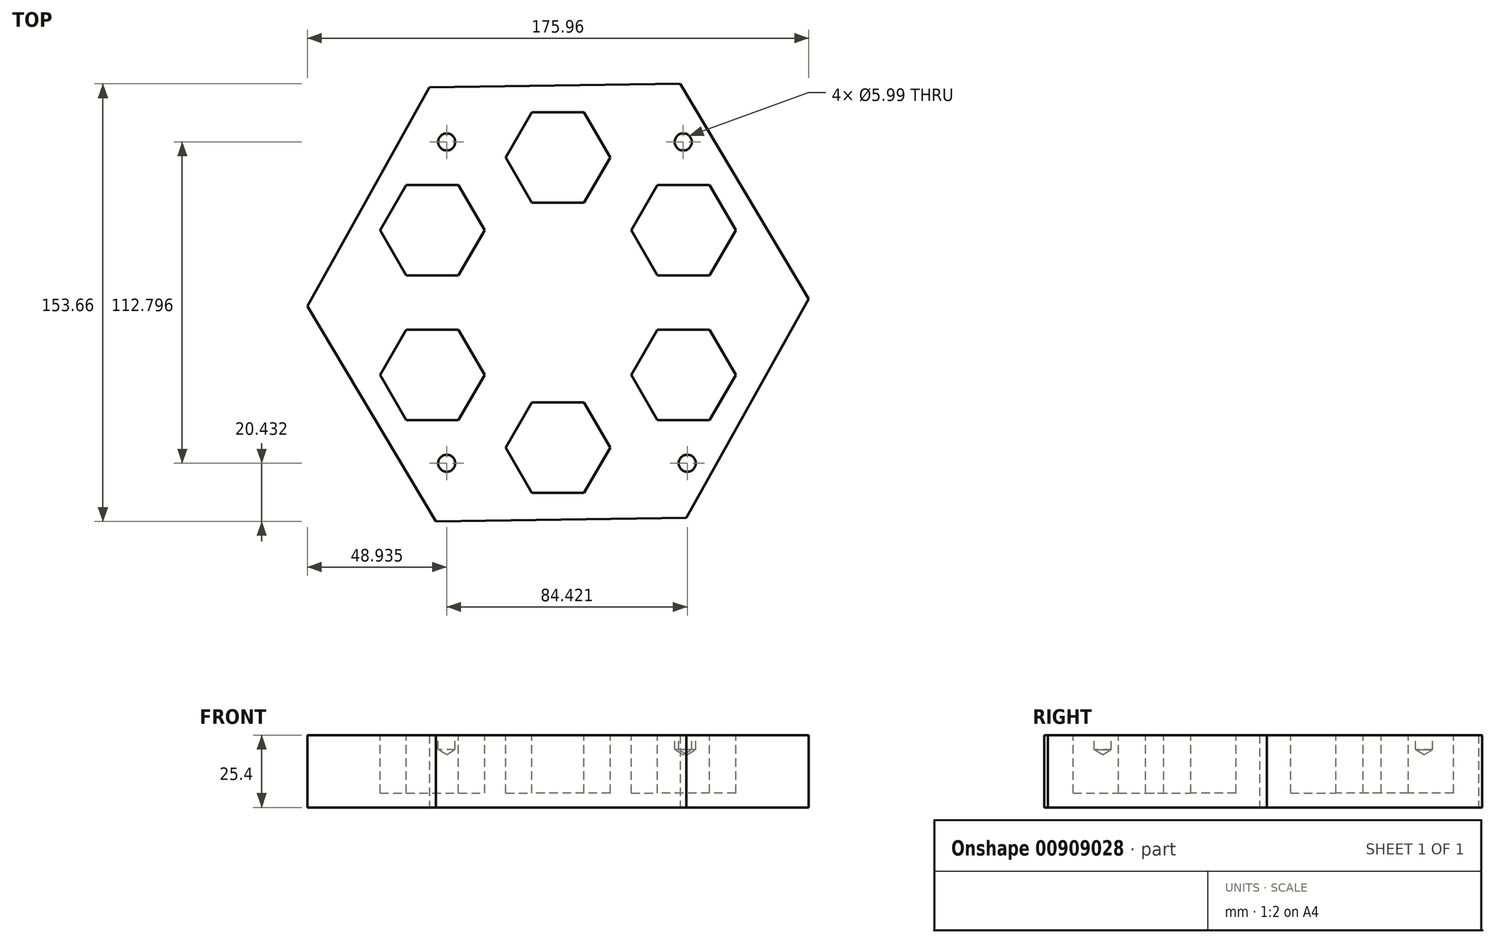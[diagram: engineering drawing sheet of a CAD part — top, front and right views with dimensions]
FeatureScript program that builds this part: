
annotation { "Feature Type Name" : "Feature", "Feature Type Description" : "" }
export const myFeature = defineFeature(function(context is Context, id is Id, definition is map)
    precondition{}
    {
        {
            var Q0;
            Q0=qCreatedBy(makeId("Top.planeOp"),FACE);
            var sketch = newSketch(context, id + "F0", { "sketchPlane" : qUnion([Q0])});
            skCircle(sketch, "E0.cCircle", {"center": v(0, 0) * mm, "radius": 76.2 * mm, "construction": true});
            skLineSegment(sketch, "E0.0", {"start": v(87.98, 1.27) * mm, "end": v(45.1, -75.56) * mm});
            skLineSegment(sketch, "E0.1", {"start": v(45.1, -75.56) * mm, "end": v(-42.89, -76.83) * mm});
            skLineSegment(sketch, "E0.2", {"start": v(-42.89, -76.83) * mm, "end": v(-87.98, -1.27) * mm});
            skLineSegment(sketch, "E0.3", {"start": v(-87.98, -1.27) * mm, "end": v(-45.1, 75.56) * mm});
            skLineSegment(sketch, "E0.4", {"start": v(-45.1, 75.56) * mm, "end": v(42.89, 76.83) * mm});
            skLineSegment(sketch, "E0.5", {"start": v(42.89, 76.83) * mm, "end": v(87.98, 1.27) * mm});
            skPoint(sketch, "E0.0.midPoint", {"position": v(66.53, -37.14) * mm});
            skSolve(sketch);
        }
        {
            var Q0;
            Q0=makeQuery(id+"F0.imprint","IMPRINT",FACE,{"disambiguationData":[TD([[makeQuery(id+"F0.imprint","IMPRINT",EDGE,{"derivedFrom":sQuery(id+"F0.wireOp",EDGE,"E0.0")}),-1.0]])]});
            extrude(context, id + "F1", {"entities" : qUnion([Q0]), "depth" : 25.4 * mm, "offsetDistance" : 25.4 * mm});
        }
        {
            var Q0;
            Q0=makeQuery(id+"F1.opExtrude","CAP_FACE",FACE,{"disambiguationData":[OSD([sQuery(id+"F0.wireOp",EDGE,"E0.0"),sQuery(id+"F0.wireOp",EDGE,"E0.1"),sQuery(id+"F0.wireOp",EDGE,"E0.2"),sQuery(id+"F0.wireOp",EDGE,"E0.3"),sQuery(id+"F0.wireOp",EDGE,"E0.4"),sQuery(id+"F0.wireOp",EDGE,"E0.5")])],"isStart":false});
            var sketch = newSketch(context, id + "F2", { "sketchPlane" : qUnion([Q0])});
            skCircle(sketch, "E1.cCircle", {"center": v(0, 50.9) * mm, "radius": 15.88 * mm, "construction": true});
            skLineSegment(sketch, "E1.0", {"start": v(9.17, 35.02) * mm, "end": v(-9.17, 35.02) * mm});
            skLineSegment(sketch, "E1.1", {"start": v(-9.17, 35.02) * mm, "end": v(-18.33, 50.9) * mm});
            skLineSegment(sketch, "E1.2", {"start": v(-18.33, 50.9) * mm, "end": v(-9.17, 66.77) * mm});
            skLineSegment(sketch, "E1.3", {"start": v(-9.17, 66.77) * mm, "end": v(9.17, 66.77) * mm});
            skLineSegment(sketch, "E1.4", {"start": v(9.17, 66.77) * mm, "end": v(18.33, 50.9) * mm});
            skLineSegment(sketch, "E1.5", {"start": v(18.33, 50.9) * mm, "end": v(9.17, 35.02) * mm});
            skPoint(sketch, "E1.0.midPoint", {"position": v(0, 35.02) * mm});
            skPoint(sketch, "E2", {"position": v(-1.1, 76.2) * mm});
            skLineSegment(sketch, "E3.1.0", {"start": v(-34.9, 41.32) * mm, "end": v(-25.74, 25.45) * mm});
            skLineSegment(sketch, "E3.1.1", {"start": v(-53.24, 41.32) * mm, "end": v(-34.9, 41.32) * mm});
            skLineSegment(sketch, "E3.1.2", {"start": v(-62.4, 25.45) * mm, "end": v(-53.24, 41.32) * mm});
            skLineSegment(sketch, "E3.1.3", {"start": v(-53.24, 9.57) * mm, "end": v(-62.4, 25.45) * mm});
            skLineSegment(sketch, "E3.1.4", {"start": v(-34.9, 9.57) * mm, "end": v(-53.24, 9.57) * mm});
            skPoint(sketch, "E3.1.5", {"position": v(-30.33, 17.5) * mm});
            skCircle(sketch, "E3.1.6", {"center": v(-44.07, 25.45) * mm, "radius": 15.88 * mm, "construction": true});
            skLineSegment(sketch, "E3.1.7", {"start": v(-25.74, 25.45) * mm, "end": v(-34.9, 9.57) * mm});
            skLineSegment(sketch, "E3.2.0", {"start": v(-53.24, -9.57) * mm, "end": v(-34.9, -9.57) * mm});
            skLineSegment(sketch, "E3.2.1", {"start": v(-62.4, -25.45) * mm, "end": v(-53.24, -9.57) * mm});
            skLineSegment(sketch, "E3.2.2", {"start": v(-53.24, -41.32) * mm, "end": v(-62.4, -25.45) * mm});
            skLineSegment(sketch, "E3.2.3", {"start": v(-34.9, -41.32) * mm, "end": v(-53.24, -41.32) * mm});
            skLineSegment(sketch, "E3.2.4", {"start": v(-25.74, -25.45) * mm, "end": v(-34.9, -41.32) * mm});
            skPoint(sketch, "E3.2.5", {"position": v(-30.33, -17.5) * mm});
            skCircle(sketch, "E3.2.6", {"center": v(-44.07, -25.45) * mm, "radius": 15.88 * mm, "construction": true});
            skLineSegment(sketch, "E3.2.7", {"start": v(-34.9, -9.57) * mm, "end": v(-25.74, -25.45) * mm});
            skLineSegment(sketch, "E3.3.0", {"start": v(-18.33, -50.9) * mm, "end": v(-9.17, -35.02) * mm});
            skLineSegment(sketch, "E3.3.1", {"start": v(-9.17, -66.77) * mm, "end": v(-18.33, -50.9) * mm});
            skLineSegment(sketch, "E3.3.2", {"start": v(9.17, -66.77) * mm, "end": v(-9.17, -66.77) * mm});
            skLineSegment(sketch, "E3.3.3", {"start": v(18.33, -50.9) * mm, "end": v(9.17, -66.77) * mm});
            skLineSegment(sketch, "E3.3.4", {"start": v(9.17, -35.02) * mm, "end": v(18.33, -50.9) * mm});
            skPoint(sketch, "E3.3.5", {"position": v(0, -35.02) * mm});
            skCircle(sketch, "E3.3.6", {"center": v(0, -50.9) * mm, "radius": 15.88 * mm, "construction": true});
            skLineSegment(sketch, "E3.3.7", {"start": v(-9.17, -35.02) * mm, "end": v(9.17, -35.02) * mm});
            skLineSegment(sketch, "E3.4.0", {"start": v(34.9, -41.32) * mm, "end": v(25.74, -25.45) * mm});
            skLineSegment(sketch, "E3.4.1", {"start": v(53.24, -41.32) * mm, "end": v(34.9, -41.32) * mm});
            skLineSegment(sketch, "E3.4.2", {"start": v(62.4, -25.45) * mm, "end": v(53.24, -41.32) * mm});
            skLineSegment(sketch, "E3.4.3", {"start": v(53.24, -9.57) * mm, "end": v(62.4, -25.45) * mm});
            skLineSegment(sketch, "E3.4.4", {"start": v(34.9, -9.57) * mm, "end": v(53.24, -9.57) * mm});
            skPoint(sketch, "E3.4.5", {"position": v(30.33, -17.5) * mm});
            skCircle(sketch, "E3.4.6", {"center": v(44.07, -25.45) * mm, "radius": 15.88 * mm, "construction": true});
            skLineSegment(sketch, "E3.4.7", {"start": v(25.74, -25.45) * mm, "end": v(34.9, -9.57) * mm});
            skLineSegment(sketch, "E3.5.0", {"start": v(53.24, 9.57) * mm, "end": v(34.9, 9.57) * mm});
            skLineSegment(sketch, "E3.5.1", {"start": v(62.4, 25.45) * mm, "end": v(53.24, 9.57) * mm});
            skLineSegment(sketch, "E3.5.2", {"start": v(53.24, 41.32) * mm, "end": v(62.4, 25.45) * mm});
            skLineSegment(sketch, "E3.5.3", {"start": v(34.9, 41.32) * mm, "end": v(53.24, 41.32) * mm});
            skLineSegment(sketch, "E3.5.4", {"start": v(25.74, 25.45) * mm, "end": v(34.9, 41.32) * mm});
            skPoint(sketch, "E3.5.5", {"position": v(30.33, 17.5) * mm});
            skCircle(sketch, "E3.5.6", {"center": v(44.07, 25.45) * mm, "radius": 15.88 * mm, "construction": true});
            skLineSegment(sketch, "E3.5.7", {"start": v(34.9, 9.57) * mm, "end": v(25.74, 25.45) * mm});
            skPoint(sketch, "E3.center", {"position": v(0, 0) * mm});
            skPoint(sketch, "E4", {"position": v(-43.73, 50.77) * mm});
            skPoint(sketch, "E5", {"position": v(43.97, 50.9) * mm});
            skPoint(sketch, "E6", {"position": v(44.07, -51.24) * mm});
            skPoint(sketch, "E6.positionSnap0", {"position": v(44.07, -41.32) * mm});
            skPoint(sketch, "E7", {"position": v(-43.73, -51.94) * mm});
            skSolve(sketch);
        }
        {
            var Q0;
            Q0=makeQuery(id+"F2.imprint","IMPRINT",FACE,{"disambiguationData":[TD([[makeQuery(id+"F2.imprint","IMPRINT",EDGE,{"derivedFrom":sQuery(id+"F2.wireOp",EDGE,"E3.1.0")}),-1.0]])]});
            var Q1;
            Q1=makeQuery(id+"F2.imprint","IMPRINT",FACE,{"disambiguationData":[TD([[makeQuery(id+"F2.imprint","IMPRINT",EDGE,{"derivedFrom":sQuery(id+"F2.wireOp",EDGE,"E1.0")}),-1.0]])]});
            var Q2;
            Q2=makeQuery(id+"F2.imprint","IMPRINT",FACE,{"disambiguationData":[TD([[makeQuery(id+"F2.imprint","IMPRINT",EDGE,{"derivedFrom":sQuery(id+"F2.wireOp",EDGE,"E3.4.0")}),-1.0]])]});
            var Q3;
            Q3=makeQuery(id+"F2.imprint","IMPRINT",FACE,{"disambiguationData":[TD([[makeQuery(id+"F2.imprint","IMPRINT",EDGE,{"derivedFrom":sQuery(id+"F2.wireOp",EDGE,"E3.5.0")}),-1.0]])]});
            var Q4;
            Q4=makeQuery(id+"F2.imprint","IMPRINT",FACE,{"disambiguationData":[TD([[makeQuery(id+"F2.imprint","IMPRINT",EDGE,{"derivedFrom":sQuery(id+"F2.wireOp",EDGE,"E3.3.0")}),-1.0]])]});
            var Q5;
            Q5=makeQuery(id+"F2.imprint","IMPRINT",FACE,{"disambiguationData":[TD([[makeQuery(id+"F2.imprint","IMPRINT",EDGE,{"derivedFrom":sQuery(id+"F2.wireOp",EDGE,"E3.2.0")}),-1.0]])]});
            extrude(context, id + "F3", {"entities" : qUnion([Q0, Q1, Q2, Q3, Q4, Q5]), "operationType" : NewBodyOperationType.REMOVE, "oppositeDirection" : true, "depth" : 20.32 * mm, "offsetDistance" : 25.4 * mm});
        }
        {
            var Q0;
            Q0=makeQuery(id+"F1.opExtrude","CAP_FACE",FACE,{"disambiguationData":[OSD([sQuery(id+"F0.wireOp",EDGE,"E0.0"),sQuery(id+"F0.wireOp",EDGE,"E0.1"),sQuery(id+"F0.wireOp",EDGE,"E0.2"),sQuery(id+"F0.wireOp",EDGE,"E0.3"),sQuery(id+"F0.wireOp",EDGE,"E0.4"),sQuery(id+"F0.wireOp",EDGE,"E0.5")])],"isStart":false});
            var sketch = newSketch(context, id + "F4", { "sketchPlane" : qUnion([Q0])});
            skPoint(sketch, "E8", {"position": v(-39.04, 56.4) * mm});
            skPoint(sketch, "E9", {"position": v(-39.04, -56.4) * mm});
            skPoint(sketch, "E10", {"position": v(45.38, -56.4) * mm});
            skPoint(sketch, "E11", {"position": v(43.97, 56.4) * mm});
            skSolve(sketch);
        }
        {
            var Q0;
            Q0=sQuery(id+"F4.wireOp",VERTEX,"E8");
            var Q1;
            Q1=sQuery(id+"F4.wireOp",VERTEX,"E11");
            var Q2;
            Q2=sQuery(id+"F4.wireOp",VERTEX,"E9");
            var Q3;
            Q3=sQuery(id+"F4.wireOp",VERTEX,"E10");
            var Q4;
            Q4=makeQuery(id+"F1.opExtrude","SWEPT_BODY",BODY,{"disambiguationData":[OSD([sQuery(id+"F0.wireOp",EDGE,"E0.0"),sQuery(id+"F0.wireOp",EDGE,"E0.1"),sQuery(id+"F0.wireOp",EDGE,"E0.2"),sQuery(id+"F0.wireOp",EDGE,"E0.3"),sQuery(id+"F0.wireOp",EDGE,"E0.4"),sQuery(id+"F0.wireOp",EDGE,"E0.5")])]});
            hole(context, id + "F5", {"style" : HoleStyle.SIMPLE, "endStyle" : HoleEndStyle.BLIND, "holeDiameter" : 6 * mm, "majorDiameter" : 6.35 * mm, "holeDepth" : 5.08 * mm, "isTappedThrough" : true, "tappedDepth" : 12.7 * mm, "tapClearance" : 3, "startFromSketch" : true, "locations" : qUnion([Q0, Q1, Q2, Q3]), "scope" : qUnion([Q4])});
        }
    });
